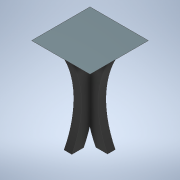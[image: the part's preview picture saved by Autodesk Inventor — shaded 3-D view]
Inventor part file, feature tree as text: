
AUTODESK INVENTOR PART (.ipt)
format: ipt  version: 2022 (Build 260153000, 153)  size: 160,256 bytes
history: native  units: mm
features: extrude x3, sketch x3, plane x2, chamfer x1, direct_edit x1, other x1
ambient origin geometry x8: Origin, YZ Plane, XZ Plane, XY Plane, X Axis, Y Axis, Z Axis, Center Point
bodies: Solid1 (feature_tree)
feature tree (11):
  extrude  "Extrusion1"  Depth=7.5mm
  plane  "Work Plane1"
  plane  "Work Plane2"
  chamfer  "Chamfer1"  Distance=1.0mm
  extrude  "Extrusion2"  Depth=10.0mm
  extrude  "Extrusion3"  Depth=10.0mm
  direct_edit  "Direct Edit1"
  sketch  "Sketch1"  dims[d0=7.5mm d1=7.5mm]
  sketch  "Sketch2"  dims[d2=0.0mm d3=1.0mm d4=0.0mm]
  sketch  "Sketch3"  dims[d5=1.0mm d6=2.0mm d7=45.0deg d8=1.5mm d9=10.0mm d10=0.0mm d11=11.0mm d12=11.0mm d13=14.79686mm d14=1.0mm d15=0.0mm d16=1.5mm d17=1.5mm d18=0.0mm d19=10.0mm d20=0.0mm d21=11.0mm d22=11.0mm d23=1.0mm d24=0.0mm d25=20.0mm d26=10.0mm d27=10.0mm]
  other  "Scale1"
